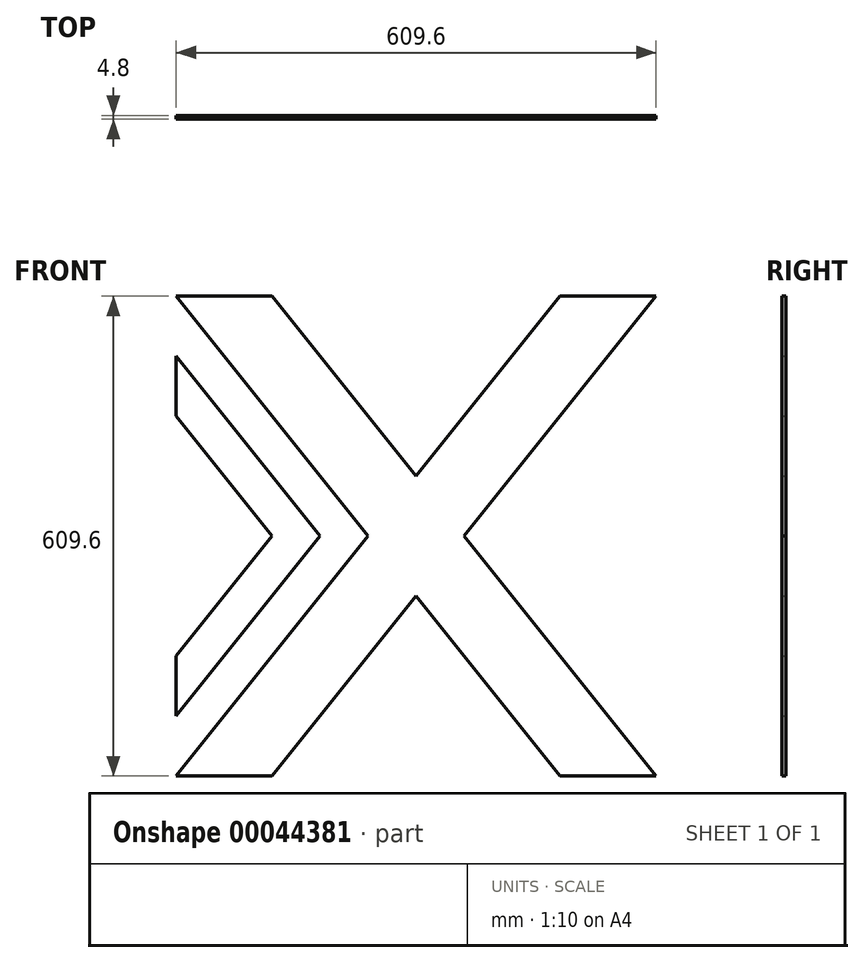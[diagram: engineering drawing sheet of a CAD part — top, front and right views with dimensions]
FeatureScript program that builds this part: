
annotation { "Feature Type Name" : "Feature", "Feature Type Description" : "" }
export const myFeature = defineFeature(function(context is Context, id is Id, definition is map)
    precondition{}
    {
        {
            assignVariable(context, id + "F0", {"name" : "Size", "anyValue" : 24});
        }
        {
            assignVariable(context, id + "F1", {"name" : "Thick", "anyValue" : .2});
        }
        {
            var Q0;
            Q0=qCreatedBy(makeId("Front.planeOp"),FACE);
            var sketch = newSketch(context, id + "F2", { "sketchPlane" : qUnion([Q0])});
            skLineSegment(sketch, "E0", {"start": v(304.8, 304.8) * mm, "end": v(182.88, 304.8) * mm});
            skLineSegment(sketch, "E1", {"start": v(182.88, 304.8) * mm, "end": v(0, 76.2) * mm});
            skLineSegment(sketch, "E2", {"start": v(304.8, 304.8) * mm, "end": v(60.96, 0) * mm});
            skLineSegment(sketch, "E3", {"start": v(-182.88, -304.8) * mm, "end": v(-304.8, -304.8) * mm});
            skLineSegment(sketch, "E4", {"start": v(-304.8, 304.8) * mm, "end": v(-182.88, 304.8) * mm});
            skLineSegment(sketch, "E5", {"start": v(-182.88, 304.8) * mm, "end": v(0, 76.2) * mm});
            skLineSegment(sketch, "E6", {"start": v(-304.8, 304.8) * mm, "end": v(-60.96, 0) * mm});
            skLineSegment(sketch, "E7", {"start": v(182.88, -304.8) * mm, "end": v(304.8, -304.8) * mm});
            skLineSegment(sketch, "E8", {"start": v(-304.8, 228.6) * mm, "end": v(-304.8, 152.4) * mm});
            skLineSegment(sketch, "E9", {"start": v(-304.8, -228.6) * mm, "end": v(-304.8, -152.4) * mm});
            skLineSegment(sketch, "E10", {"start": v(-304.8, 152.4) * mm, "end": v(-182.88, 0) * mm});
            skLineSegment(sketch, "E11", {"start": v(-182.88, 0) * mm, "end": v(-304.8, -152.4) * mm});
            skLineSegment(sketch, "E12", {"start": v(-304.8, -228.6) * mm, "end": v(-121.92, 0) * mm});
            skLineSegment(sketch, "E13", {"start": v(-121.92, 0) * mm, "end": v(-304.8, 228.6) * mm});
            skLineSegment(sketch, "E14.trimOffspring", {"start": v(60.96, 0) * mm, "end": v(304.8, -304.8) * mm});
            skLineSegment(sketch, "E15.trimOffspring", {"start": v(0, -76.2) * mm, "end": v(-182.88, -304.8) * mm});
            skLineSegment(sketch, "E16.trimOffspring", {"start": v(0, -76.2) * mm, "end": v(182.88, -304.8) * mm});
            skLineSegment(sketch, "E17.trimOffspring", {"start": v(-60.96, 0) * mm, "end": v(-304.8, -304.8) * mm});
            skSolve(sketch);
        }
        {
            var Q0;
            {var subQ9=sQuery(id+"F2.wireOp",EDGE,"E1");Q0=makeQuery(id+"F2.imprint","IMPRINT",FACE,{"disambiguationData":[TD([[makeQuery(id+"F2.imprint","IMPRINT",EDGE,{"derivedFrom":subQ9}),1.0]])]});}
            var Q1;
            {var subQ3=sQuery(id+"F2.wireOp",EDGE,"E10");Q1=makeQuery(id+"F2.imprint","IMPRINT",FACE,{"disambiguationData":[TD([[makeQuery(id+"F2.imprint","IMPRINT",EDGE,{"derivedFrom":subQ3}),1.0]])]});}
            extrude(context, id + "F3", {"entities" : qUnion([Q0, Q1]), "depth" : (getVariable(context, 'Size') * getVariable(context, 'Thick')) * mm});
        }
    });
